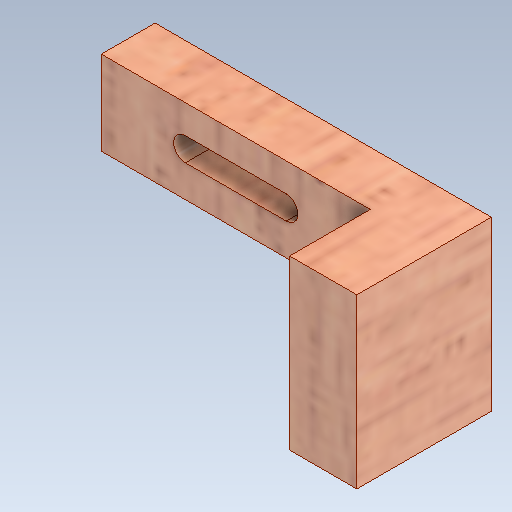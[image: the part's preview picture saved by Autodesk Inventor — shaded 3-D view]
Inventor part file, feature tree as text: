
AUTODESK INVENTOR PART (.ipt)
format: ipt  version: 2020 (Build 240168000, 168)  size: 267,264 bytes
history: native  units: mm
features: extrude x4, sketch x4, fillet x1, mirror x1
ambient origin geometry x8: Origin, YZ Plane, XZ Plane, XY Plane, X Axis, Y Axis, Z Axis, Center Point
bodies: Solid1 (feature_tree)
feature tree (10):
  extrude  "Extrusion1"  Depth=25.0mm
  extrude  "Extrusion5"  Depth=3.5mm
  extrude  "Extrusion6"  Depth=6.0mm
  extrude  "Extrusion7"  Depth=2.0mm
  fillet  "Fillet2"  Radius=15.0mm
  mirror  "Mirror1"
  sketch  "Sketch1"  dims[d0=50.0mm d1=25.0mm]
  sketch  "Sketch5"  dims[d2=20.0mm d3=0.0mm d29=3.5mm]
  sketch  "Sketch6"  dims[d30=4.0mm d31=6.0mm]
  sketch  "Sketch7"  dims[d32=20.0mm d33=15.0mm d34=15.0mm d35=0.0mm d36=10.0mm d37=10.0mm d38=0.0mm d40=12.0mm d41=0.0mm d42=2.0mm]
